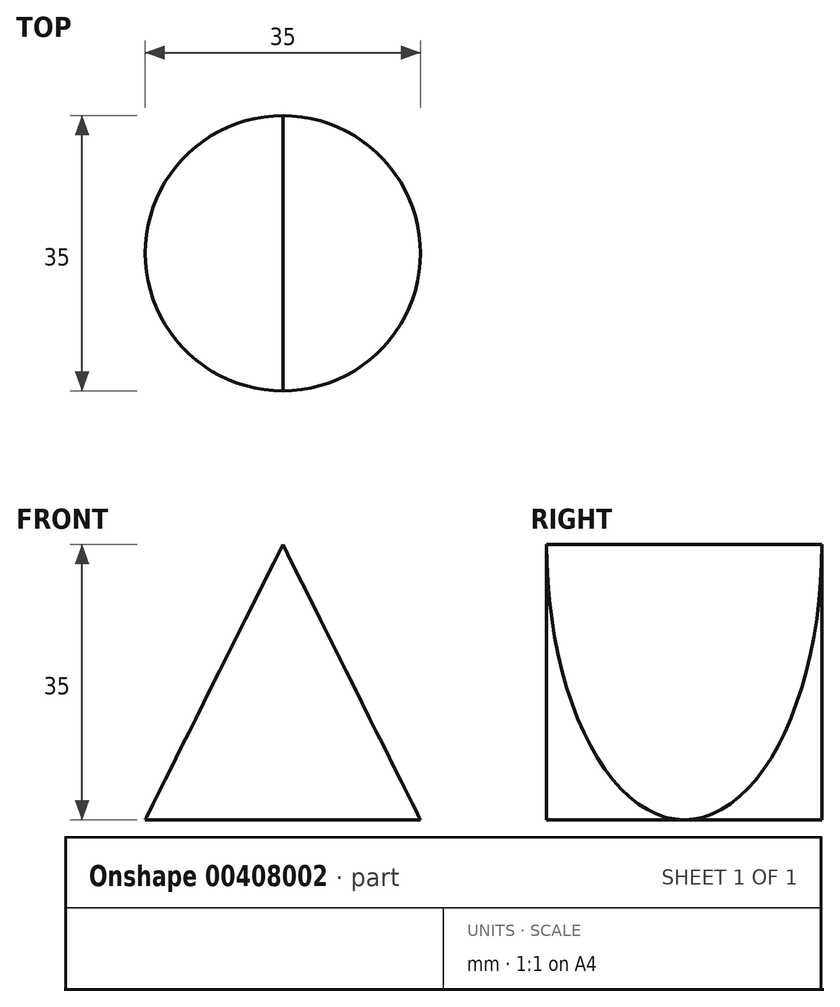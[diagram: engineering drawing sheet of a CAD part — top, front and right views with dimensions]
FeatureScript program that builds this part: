
annotation { "Feature Type Name" : "Feature", "Feature Type Description" : "" }
export const myFeature = defineFeature(function(context is Context, id is Id, definition is map)
    precondition{}
    {
        {
            var Q0;
            Q0=qCreatedBy(makeId("Top.planeOp"),FACE);
            var sketch = newSketch(context, id + "F0", { "sketchPlane" : qUnion([Q0])});
            skCircle(sketch, "E0", {"center": v(0, 0) * mm, "radius": 17.5 * mm});
            skSolve(sketch);
        }
        {
            var Q0;
            Q0=makeQuery(id+"F0.imprint","IMPRINT",FACE,{"disambiguationData":[TD([[makeQuery(id+"F0.imprint","IMPRINT",EDGE,{"derivedFrom":sQuery(id+"F0.wireOp",EDGE,"E0")}),1.0]])]});
            extrude(context, id + "F1", {"entities" : qUnion([Q0]), "depth" : 35 * mm});
        }
        {
            var Q0;
            Q0=qCreatedBy(makeId("Front.planeOp"),FACE);
            var sketch = newSketch(context, id + "F2", { "sketchPlane" : qUnion([Q0])});
            skLineSegment(sketch, "E1.0", {"start": v(-17.5, 0) * mm, "end": v(17.5, 0) * mm});
            skLineSegment(sketch, "E2.0", {"start": v(-17.5, 35) * mm, "end": v(17.5, 35) * mm});
            skLineSegment(sketch, "E3", {"start": v(-17.5, 0) * mm, "end": v(0, 35) * mm});
            skLineSegment(sketch, "E4", {"start": v(0, 35) * mm, "end": v(17.5, 0) * mm});
            skSolve(sketch);
        }
        {
            var Q0;
            Q0=makeQuery(id+"F2.imprint","IMPRINT",FACE,{"disambiguationData":[TD([[makeQuery(id+"F2.imprint","IMPRINT",EDGE,{"derivedFrom":sQuery(id+"F2.wireOp",EDGE,"E1.0")}),1.0]])]});
            extrude(context, id + "F3", {"entities" : qUnion([Q0]), "endBound" : BoundingType.SYMMETRIC, "depth" : 50 * mm});
        }
        {
            var Q0;
            Q0=makeQuery(id+"F1.opExtrude","SWEPT_BODY",BODY,{"disambiguationData":[OSD([sQuery(id+"F0.wireOp",EDGE,"E0")])]});
            var Q1;
            Q1=makeQuery(id+"F3.opExtrude","SWEPT_BODY",BODY,{"disambiguationData":[OSD([sQuery(id+"F2.wireOp",EDGE,"E1.0"),sQuery(id+"F2.wireOp",EDGE,"E3"),sQuery(id+"F2.wireOp",EDGE,"E4")])]});
            booleanBodies(context, id + "F4", {"operationType" : BooleanOperationType.INTERSECTION, "tools" : qUnion([Q0, Q1])});
        }
    });
